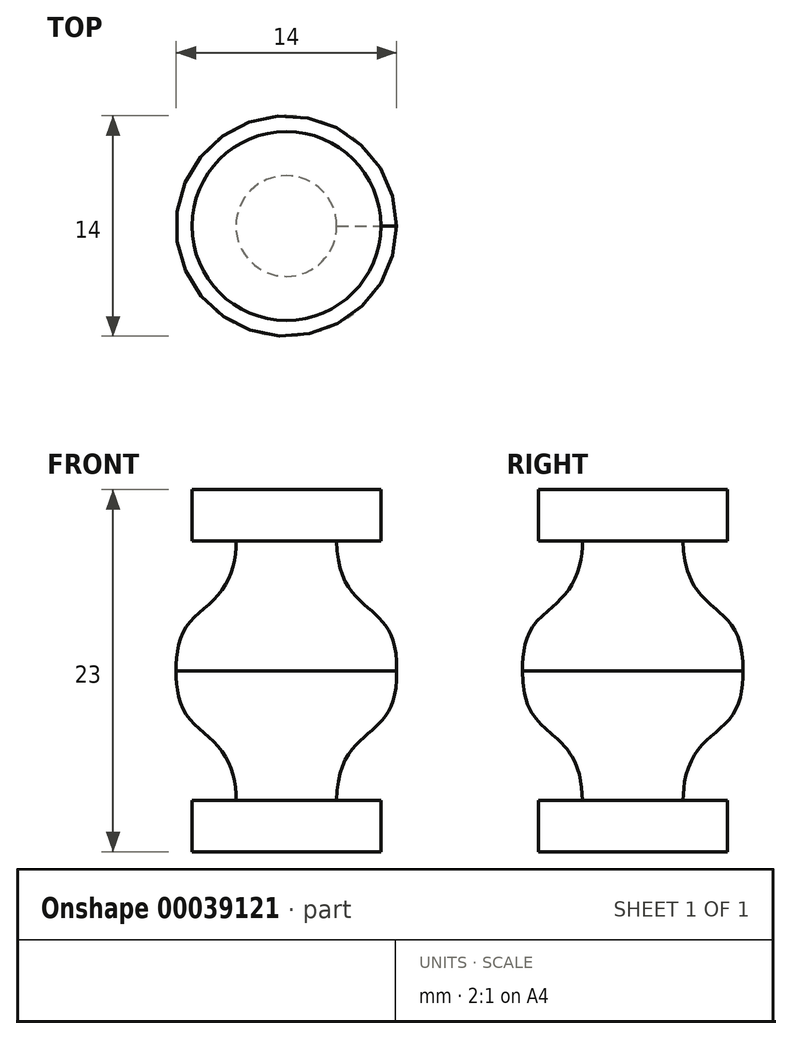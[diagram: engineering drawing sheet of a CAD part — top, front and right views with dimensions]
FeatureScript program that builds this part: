
annotation { "Feature Type Name" : "Feature", "Feature Type Description" : "" }
export const myFeature = defineFeature(function(context is Context, id is Id, definition is map)
    precondition{}
    {
        {
            var Q0;
            Q0=qCreatedBy(makeId("Front.planeOp"),FACE);
            var sketch = newSketch(context, id + "F0", { "sketchPlane" : qUnion([Q0])});
            skLineSegment(sketch, "E0", {"start": v(0, 0) * mm, "end": v(6, 0) * mm});
            skLineSegment(sketch, "E1", {"start": v(6, 0) * mm, "end": v(6, -3.25) * mm});
            skLineSegment(sketch, "E2", {"start": v(6, -3.25) * mm, "end": v(3.2, -3.25) * mm});
            skLineSegment(sketch, "E3", {"start": v(3.2, -19.75) * mm, "end": v(6, -19.75) * mm});
            skLineSegment(sketch, "E4", {"start": v(6, -19.75) * mm, "end": v(6, -23) * mm});
            skLineSegment(sketch, "E5", {"start": v(6, -23) * mm, "end": v(0, -23) * mm});
            skLineSegment(sketch, "E6", {"start": v(0, 1.74) * mm, "end": v(0, -22.73) * mm, "construction": true});
            skLineSegment(sketch, "E7", {"start": v(0, 0) * mm, "end": v(0, -23) * mm});
            skLineSegment(sketch, "E8", {"start": v(-3.95, -11.5) * mm, "end": v(10.2, -11.5) * mm, "construction": true});
            skFitSpline(sketch, "E9", {"points": [v(3.2, -19.75) * mm, v(5.45, -15.26) * mm, v(7, -11.5) * mm], "startDerivative": vector(0, 15.55) * mm, "endDerivative": vector(-0.18, 14.03) * mm});
            skFitSpline(sketch, "E10.MirrorCS", {"points": [v(3.2, -3.25) * mm, v(5.45, -7.74) * mm, v(7, -11.5) * mm], "startDerivative": vector(0, -15.55) * mm, "endDerivative": vector(-0.18, -14.03) * mm});
            skSolve(sketch);
        }
        {
            var Q0;
            Q0=makeQuery(id+"F0.imprint","IMPRINT",FACE,{"disambiguationData":[TD([[makeQuery(id+"F0.imprint","IMPRINT",EDGE,{"derivedFrom":sQuery(id+"F0.wireOp",EDGE,"E0")}),-1.0]])]});
            var Q1;
            Q1=sQuery(id+"F0.wireOp",EDGE,"E6");
            revolve(context, id + "F1", {"entities" : qUnion([Q0]), "axis" : qUnion([Q1]), "revolveType" : RevolveType.FULL});
        }
    });
